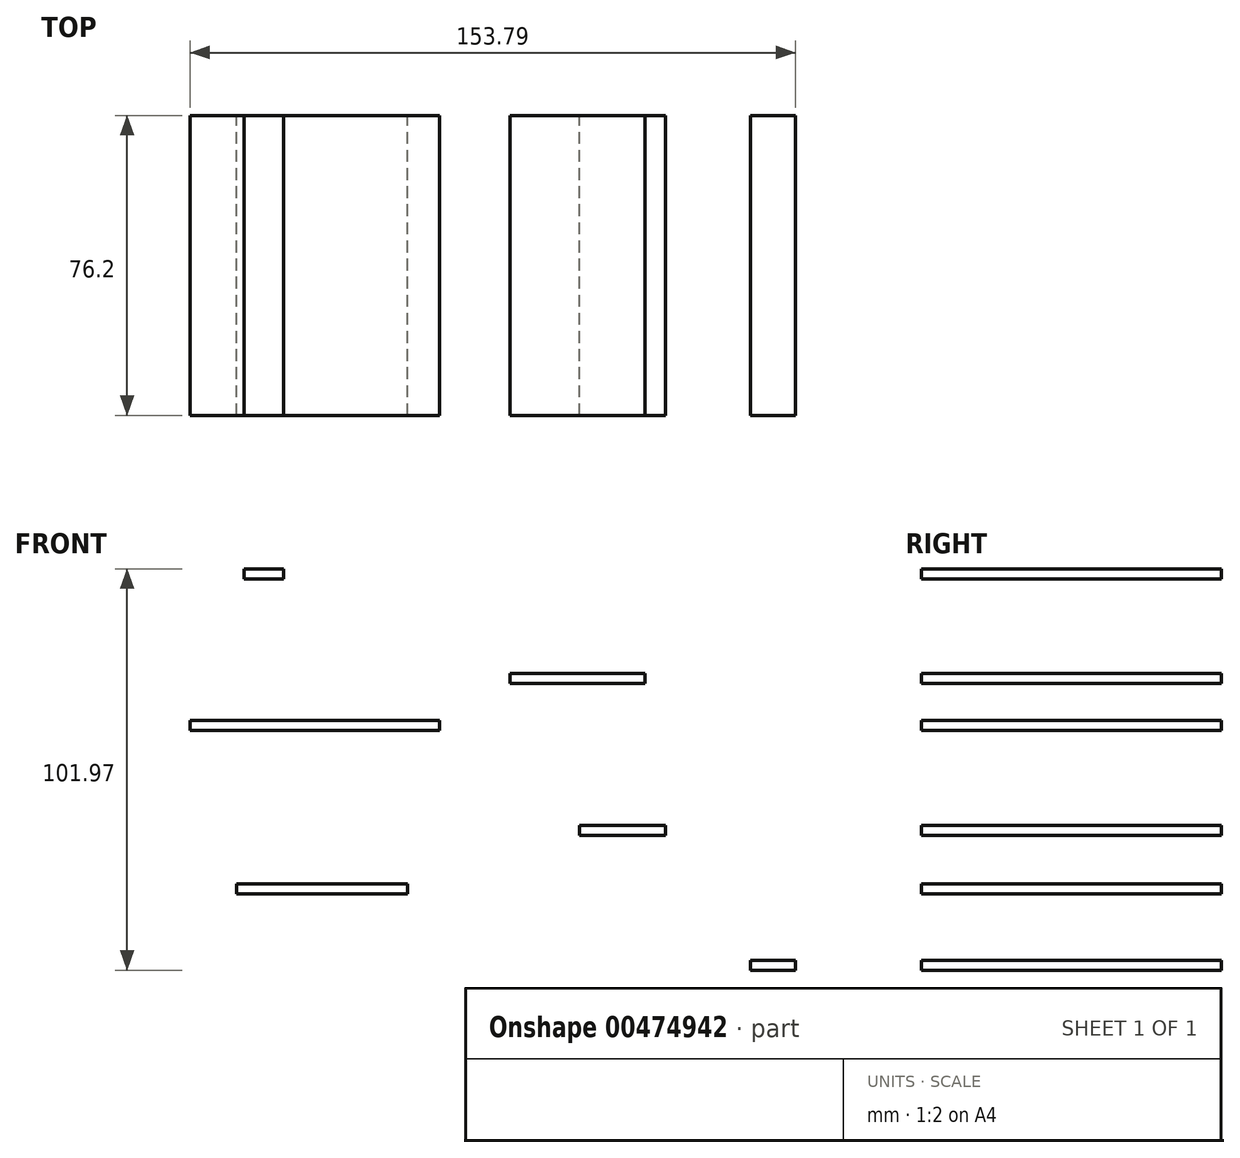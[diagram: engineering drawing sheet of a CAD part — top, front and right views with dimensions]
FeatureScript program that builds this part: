
annotation { "Feature Type Name" : "Feature", "Feature Type Description" : "" }
export const myFeature = defineFeature(function(context is Context, id is Id, definition is map)
    precondition{}
    {
        {
            var Q0;
            Q0=qCreatedBy(makeId("Front.planeOp"),FACE);
            var sketch = newSketch(context, id + "F0", { "sketchPlane" : qUnion([Q0])});
            skLineSegment(sketch, "E0", {"start": v(-72.53, -25.73) * mm, "end": v(-29.1, -25.73) * mm});
            skLineSegment(sketch, "E1", {"start": v(-84.3, 15.84) * mm, "end": v(-20.97, 15.84) * mm});
            skLineSegment(sketch, "E2", {"start": v(-2.98, 27.67) * mm, "end": v(31.26, 27.67) * mm});
            skLineSegment(sketch, "E3", {"start": v(58.04, -45.12) * mm, "end": v(69.5, -45.12) * mm});
            skLineSegment(sketch, "E4", {"start": v(14.68, -10.83) * mm, "end": v(36.45, -10.83) * mm});
            skLineSegment(sketch, "E5", {"start": v(-70.64, 56.85) * mm, "end": v(-60.5, 56.85) * mm});
            skLineSegment(sketch, "E6.0", {"start": v(-70.64, 54.3) * mm, "end": v(-60.5, 54.3) * mm});
            skLineSegment(sketch, "E7.0", {"start": v(-2.98, 30.21) * mm, "end": v(31.26, 30.21) * mm});
            skLineSegment(sketch, "E8.0", {"start": v(-84.3, 18.38) * mm, "end": v(-20.97, 18.38) * mm});
            skLineSegment(sketch, "E9.0", {"start": v(-72.53, -23.19) * mm, "end": v(-29.1, -23.19) * mm});
            skLineSegment(sketch, "E10.0", {"start": v(14.68, -8.29) * mm, "end": v(36.45, -8.29) * mm});
            skLineSegment(sketch, "E11.0", {"start": v(58.04, -42.58) * mm, "end": v(69.5, -42.58) * mm});
            skLineSegment(sketch, "E12", {"start": v(-60.5, 56.85) * mm, "end": v(-60.5, 54.3) * mm});
            skLineSegment(sketch, "E13", {"start": v(-70.64, 56.85) * mm, "end": v(-70.64, 54.3) * mm});
            skLineSegment(sketch, "E14", {"start": v(-20.97, 18.38) * mm, "end": v(-20.97, 15.84) * mm});
            skLineSegment(sketch, "E15", {"start": v(-84.3, 18.38) * mm, "end": v(-84.3, 15.84) * mm});
            skLineSegment(sketch, "E16", {"start": v(-72.53, -23.19) * mm, "end": v(-72.53, -25.73) * mm});
            skLineSegment(sketch, "E17", {"start": v(-29.1, -23.19) * mm, "end": v(-29.1, -25.73) * mm});
            skLineSegment(sketch, "E18", {"start": v(-2.98, 30.21) * mm, "end": v(-2.98, 27.67) * mm});
            skLineSegment(sketch, "E19", {"start": v(31.26, 30.21) * mm, "end": v(31.26, 27.67) * mm});
            skLineSegment(sketch, "E20", {"start": v(36.45, -8.29) * mm, "end": v(36.45, -10.83) * mm});
            skLineSegment(sketch, "E21", {"start": v(14.68, -8.29) * mm, "end": v(14.68, -10.83) * mm});
            skLineSegment(sketch, "E22", {"start": v(69.5, -45.12) * mm, "end": v(69.5, -42.58) * mm});
            skLineSegment(sketch, "E23", {"start": v(58.04, -42.58) * mm, "end": v(58.04, -45.12) * mm});
            skSolve(sketch);
        }
        {
            var Q0;
            Q0 = qSketchRegion(id + "F0", true);
            extrude(context, id + "F1", {"entities" : qUnion([Q0]), "depth" : 76.2 * mm});
        }
    });
